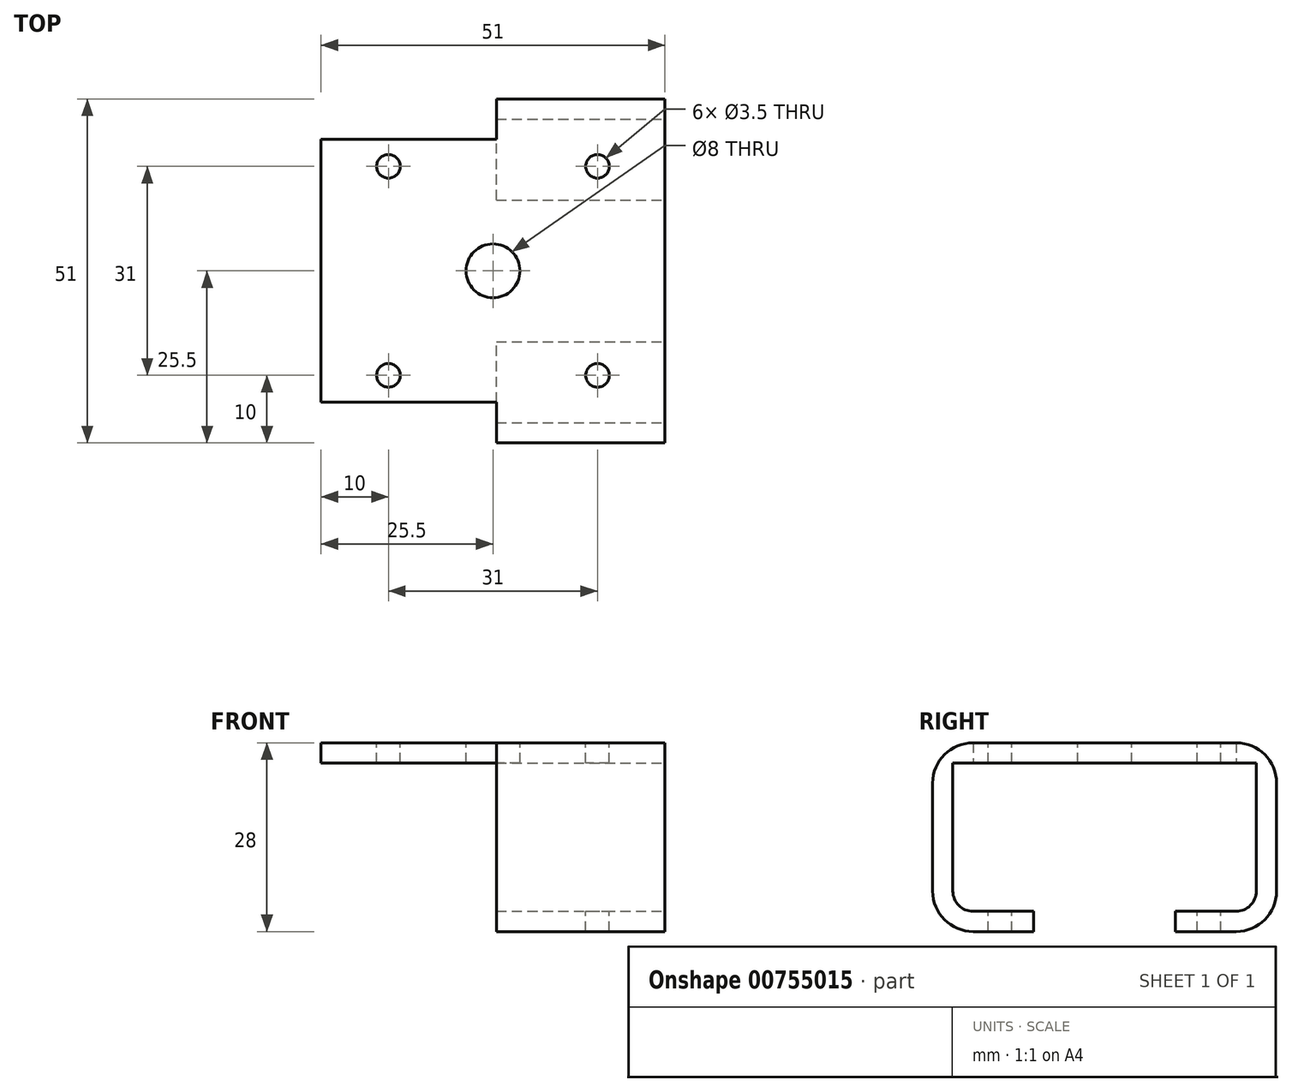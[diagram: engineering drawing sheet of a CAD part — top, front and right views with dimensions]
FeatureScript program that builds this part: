
annotation { "Feature Type Name" : "Feature", "Feature Type Description" : "" }
export const myFeature = defineFeature(function(context is Context, id is Id, definition is map)
    precondition{}
    {
        {
            var Q0;
            Q0=qCreatedBy(makeId("Top.planeOp"),FACE);
            var sketch = newSketch(context, id + "F0", { "sketchPlane" : qUnion([Q0])});
            skLineSegment(sketch, "E0.bottom", {"start": v(0, 0) * mm, "end": v(-25, 0) * mm});
            skLineSegment(sketch, "E0.top", {"start": v(0, 51) * mm, "end": v(-25, 51) * mm});
            skLineSegment(sketch, "E0.left", {"start": v(0, 0) * mm, "end": v(0, 51) * mm});
            skLineSegment(sketch, "E0.right", {"start": v(-51, 6) * mm, "end": v(-51, 45) * mm});
            skLineSegment(sketch, "E1.bottom", {"start": v(-51, 6) * mm, "end": v(-25, 6) * mm});
            skLineSegment(sketch, "E1.right", {"start": v(-25, 6) * mm, "end": v(-25, 0) * mm});
            skLineSegment(sketch, "E2.top", {"start": v(-51, 45) * mm, "end": v(-25, 45) * mm});
            skLineSegment(sketch, "E2.right", {"start": v(-25, 51) * mm, "end": v(-25, 45) * mm});
            skSolve(sketch);
        }
        {
            var Q0;
            Q0=makeQuery(id+"F0.imprint","IMPRINT",FACE,{"disambiguationData":[TD([[makeQuery(id+"F0.imprint","IMPRINT",EDGE,{"derivedFrom":sQuery(id+"F0.wireOp",EDGE,"E0.bottom")}),-1.0]])]});
            extrude(context, id + "F1", {"entities" : qUnion([Q0]), "depth" : 3 * mm, "offsetDistance" : 25 * mm});
        }
        {
            var Q0;
            Q0=qCreatedBy(makeId("Right.planeOp"),FACE);
            var sketch = newSketch(context, id + "F2", { "sketchPlane" : qUnion([Q0])});
            skLineSegment(sketch, "E3.bottom", {"start": v(0, 0) * mm, "end": v(3, 0) * mm});
            skLineSegment(sketch, "E3.top", {"start": v(0, -25) * mm, "end": v(3, -25) * mm});
            skLineSegment(sketch, "E3.left", {"start": v(0, 0) * mm, "end": v(0, -25) * mm});
            skLineSegment(sketch, "E3.right", {"start": v(3, 0) * mm, "end": v(3, -25) * mm});
            skSolve(sketch);
        }
        {
            var Q0;
            Q0=qSketchRegion(id+"F2",true);
            extrude(context, id + "F3", {"entities" : qUnion([Q0]), "operationType" : NewBodyOperationType.ADD, "oppositeDirection" : true, "depth" : 25 * mm, "offsetDistance" : 25 * mm});
        }
        {
            var Q0;
            Q0=qCreatedBy(makeId("Right.planeOp"),FACE);
            var sketch = newSketch(context, id + "F4", { "sketchPlane" : qUnion([Q0])});
            skLineSegment(sketch, "E4.bottom", {"start": v(48, 0) * mm, "end": v(51, 0) * mm});
            skLineSegment(sketch, "E4.top", {"start": v(48, -25) * mm, "end": v(51, -25) * mm});
            skLineSegment(sketch, "E4.left", {"start": v(48, 0) * mm, "end": v(48, -25) * mm});
            skLineSegment(sketch, "E4.right", {"start": v(51, 0) * mm, "end": v(51, -25) * mm});
            skSolve(sketch);
        }
        {
            var Q0;
            Q0=qSketchRegion(id+"F4",true);
            extrude(context, id + "F5", {"entities" : qUnion([Q0]), "operationType" : NewBodyOperationType.ADD, "oppositeDirection" : true, "depth" : 25 * mm, "offsetDistance" : 25 * mm});
        }
        {
            var Q0;
            Q0=makeQuery(id+"F3.opExtrude","SWEPT_FACE",FACE,{"disambiguationData":[OSD([sQuery(id+"F2.wireOp",EDGE,"E3.top")])]});
            var sketch = newSketch(context, id + "F6", { "sketchPlane" : qUnion([Q0])});
            skLineSegment(sketch, "E5.bottom", {"start": v(-25, -15) * mm, "end": v(0, -15) * mm});
            skLineSegment(sketch, "E5.top", {"start": v(-25, 0) * mm, "end": v(0, 0) * mm});
            skLineSegment(sketch, "E5.left", {"start": v(-25, -15) * mm, "end": v(-25, 0) * mm});
            skLineSegment(sketch, "E5.right", {"start": v(0, -15) * mm, "end": v(0, 0) * mm});
            skSolve(sketch);
        }
        {
            var Q0;
            Q0=qSketchRegion(id+"F6",true);
            extrude(context, id + "F7", {"entities" : qUnion([Q0]), "operationType" : NewBodyOperationType.ADD, "oppositeDirection" : true, "depth" : 3 * mm, "offsetDistance" : 25 * mm});
        }
        {
            var Q0;
            Q0=makeQuery(id+"F5.opExtrude","SWEPT_FACE",FACE,{"disambiguationData":[OSD([sQuery(id+"F4.wireOp",EDGE,"E4.top")])]});
            var sketch = newSketch(context, id + "F8", { "sketchPlane" : qUnion([Q0])});
            skLineSegment(sketch, "E6.bottom", {"start": v(-25, -36) * mm, "end": v(0, -36) * mm});
            skLineSegment(sketch, "E6.top", {"start": v(-25, -51) * mm, "end": v(0, -51) * mm});
            skLineSegment(sketch, "E6.left", {"start": v(-25, -36) * mm, "end": v(-25, -51) * mm});
            skLineSegment(sketch, "E6.right", {"start": v(0, -36) * mm, "end": v(0, -51) * mm});
            skSolve(sketch);
        }
        {
            var Q0;
            Q0=qSketchRegion(id+"F8",true);
            extrude(context, id + "F9", {"entities" : qUnion([Q0]), "operationType" : NewBodyOperationType.ADD, "oppositeDirection" : true, "depth" : 3 * mm, "offsetDistance" : 25 * mm});
        }
        {
            var Q0;
            Q0=makeQuery(id+"F1.opExtrude","CAP_FACE",FACE,{"disambiguationData":[OSD([sQuery(id+"F0.wireOp",EDGE,"E0.bottom"),sQuery(id+"F0.wireOp",EDGE,"E0.top"),sQuery(id+"F0.wireOp",EDGE,"E0.left"),sQuery(id+"F0.wireOp",EDGE,"E0.right")])],"isStart":false});
            var sketch = newSketch(context, id + "F10", { "sketchPlane" : qUnion([Q0])});
            skPoint(sketch, "E7", {"position": v(-41, 41) * mm});
            skPoint(sketch, "E8", {"position": v(-10, 41) * mm});
            skPoint(sketch, "E9", {"position": v(-10, 10) * mm});
            skPoint(sketch, "E10", {"position": v(-41, 10) * mm});
            skSolve(sketch);
        }
        {
            var Q0;
            Q0=sQuery(id+"F10.wireOp",VERTEX,"E7");
            var Q1;
            Q1=sQuery(id+"F10.wireOp",VERTEX,"E8");
            var Q2;
            Q2=sQuery(id+"F10.wireOp",VERTEX,"E9");
            var Q3;
            Q3=sQuery(id+"F10.wireOp",VERTEX,"E10");
            var Q4;
            Q4=makeQuery(id+"F1.opExtrude","SWEPT_BODY",BODY,{"disambiguationData":[OSD([sQuery(id+"F0.wireOp",EDGE,"E0.bottom"),sQuery(id+"F0.wireOp",EDGE,"E0.top"),sQuery(id+"F0.wireOp",EDGE,"E0.left"),sQuery(id+"F0.wireOp",EDGE,"E0.right")])]});
            hole(context, id + "F11", {"style" : HoleStyle.SIMPLE, "endStyle" : HoleEndStyle.THROUGH, "holeDiameter" : 3.5 * mm, "majorDiameter" : 5 * mm, "isTappedThrough" : true, "tappedDepth" : 12 * mm, "tapClearance" : 3, "locations" : qUnion([Q0, Q1, Q2, Q3]), "scope" : qUnion([Q4])});
        }
        {
            var Q0;
            Q0=makeQuery(id+"F1.opExtrude","CAP_FACE",FACE,{"disambiguationData":[OSD([sQuery(id+"F0.wireOp",EDGE,"E0.bottom"),sQuery(id+"F0.wireOp",EDGE,"E0.top"),sQuery(id+"F0.wireOp",EDGE,"E0.left"),sQuery(id+"F0.wireOp",EDGE,"E0.right")])],"isStart":false});
            var sketch = newSketch(context, id + "F12", { "sketchPlane" : qUnion([Q0])});
            skPoint(sketch, "E11", {"position": v(-25.5, 25.5) * mm});
            skSolve(sketch);
        }
        {
            var Q0;
            Q0=sQuery(id+"F12.wireOp",VERTEX,"E11");
            var Q1;
            Q1=makeQuery(id+"F1.opExtrude","SWEPT_BODY",BODY,{"disambiguationData":[OSD([sQuery(id+"F0.wireOp",EDGE,"E0.bottom"),sQuery(id+"F0.wireOp",EDGE,"E0.top"),sQuery(id+"F0.wireOp",EDGE,"E0.left"),sQuery(id+"F0.wireOp",EDGE,"E0.right")])]});
            hole(context, id + "F13", {"style" : HoleStyle.SIMPLE, "endStyle" : HoleEndStyle.THROUGH, "holeDiameter" : 8 * mm, "majorDiameter" : 5 * mm, "isTappedThrough" : true, "tappedDepth" : 12 * mm, "tapClearance" : 3, "locations" : qUnion([Q0]), "scope" : qUnion([Q1])});
        }
        {
            var Q0;
            Q0=makeQuery(id+"F3.opExtrude","SWEPT_EDGE",EDGE,{"disambiguationData":[OSD([sQuery(id+"F2.wireOp",EDGE,"E3.bottom"),sQuery(id+"F2.wireOp",EDGE,"E3.right")])]});
            var Q1;
            Q1=makeQuery(id+"F5.opExtrude","SWEPT_EDGE",EDGE,{"disambiguationData":[OSD([sQuery(id+"F4.wireOp",EDGE,"E4.bottom"),sQuery(id+"F4.wireOp",EDGE,"E4.left")])]});
            var Q2;
            Q2=makeQuery(id+"F9.boolean.opBoolean","INTERSECT",EDGE,{"derivedFrom":[makeQuery(id+"F5.opExtrude","SWEPT_FACE",FACE,{"disambiguationData":[OSD([sQuery(id+"F4.wireOp",EDGE,"E4.left")])]}),makeQuery(id+"F9.opExtrude","CAP_FACE",FACE,{"disambiguationData":[OSD([sQuery(id+"F8.wireOp",EDGE,"E6.bottom"),sQuery(id+"F8.wireOp",EDGE,"E6.top"),sQuery(id+"F8.wireOp",EDGE,"E6.left"),sQuery(id+"F8.wireOp",EDGE,"E6.right")])],"isStart":false})]});
            var Q3;
            Q3=makeQuery(id+"F7.boolean.opBoolean","INTERSECT",EDGE,{"derivedFrom":[makeQuery(id+"F3.opExtrude","SWEPT_FACE",FACE,{"disambiguationData":[OSD([sQuery(id+"F2.wireOp",EDGE,"E3.right")])]}),makeQuery(id+"F7.opExtrude","CAP_FACE",FACE,{"disambiguationData":[OSD([sQuery(id+"F6.wireOp",EDGE,"E5.bottom"),sQuery(id+"F6.wireOp",EDGE,"E5.top"),sQuery(id+"F6.wireOp",EDGE,"E5.left"),sQuery(id+"F6.wireOp",EDGE,"E5.right")])],"isStart":false})]});
            fillet(context, id + "F14", {"entities" : qUnion([Q0, Q1, Q2, Q3]), "radius" : 3 * mm, "tangentPropagation" : true, "allowEdgeOverflow" : false});
        }
        {
            var Q0;
            Q0=makeQuery(id+"F1.opExtrude","CAP_EDGE",EDGE,{"disambiguationData":[OSD([sQuery(id+"F0.wireOp",EDGE,"E0.bottom")])],"isStart":false});
            var Q1;
            Q1=makeQuery(id+"F3.opExtrude","SWEPT_EDGE",EDGE,{"disambiguationData":[OSD([sQuery(id+"F2.wireOp",EDGE,"E3.top"),sQuery(id+"F2.wireOp",EDGE,"E3.left")])]});
            var Q2;
            Q2=makeQuery(id+"F1.opExtrude","CAP_EDGE",EDGE,{"disambiguationData":[OSD([sQuery(id+"F0.wireOp",EDGE,"E0.top")])],"isStart":false});
            var Q3;
            Q3=makeQuery(id+"F5.opExtrude","SWEPT_EDGE",EDGE,{"disambiguationData":[OSD([sQuery(id+"F4.wireOp",EDGE,"E4.top"),sQuery(id+"F4.wireOp",EDGE,"E4.right")])]});
            fillet(context, id + "F15", {"entities" : qUnion([Q0, Q1, Q2, Q3]), "radius" : 6 * mm, "tangentPropagation" : true, "allowEdgeOverflow" : false});
        }
    });
